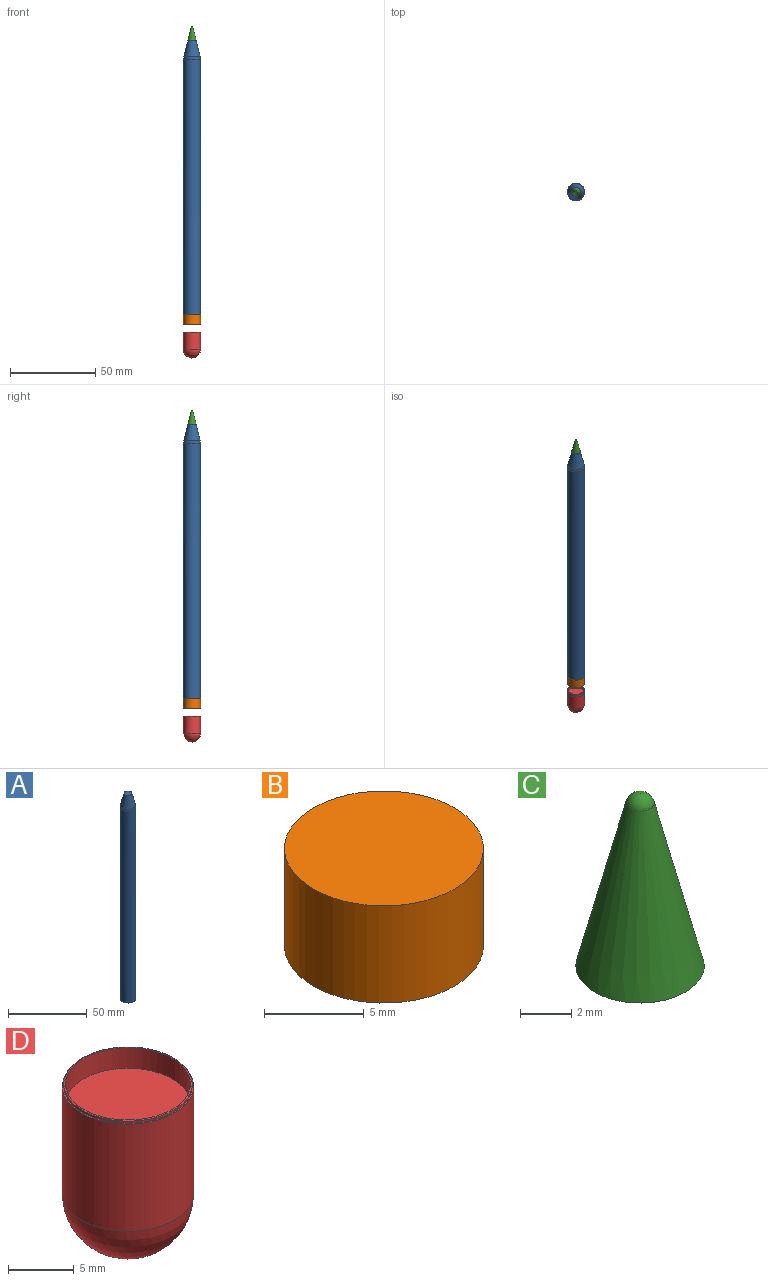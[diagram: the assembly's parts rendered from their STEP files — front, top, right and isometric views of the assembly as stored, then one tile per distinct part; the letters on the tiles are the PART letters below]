
ASSEMBLY  parts=4 mates=3
PART A: 5 faces, bbox 10x10x160 mm
  f0: cylinder r=5mm len=149.26mm, axis (0,0,-1), area 4689.2mm2, adj f1,f4
  f1: plane 10x10mm, normal (0,0,-1), area 78.5mm2, adj f0
  f2: plane 5x5mm, normal (0,0,1), area 19.6mm2, adj f3
  f3: cone r=5mm half-angle=14deg, axis (0,0,-1), area 220.1mm2, adj f2,f4
  f4: revolved ~10x10mm, area 91.2mm2, adj f0,f3
PART B: 106 faces, bbox 10x10x6 mm
  f0: cylinder r=5mm len=10mm, axis (0,0,-1), area 179.7mm2, adj f1,f6,f13,f14,f15,f16,f17,f18
  f1: plane 10x10mm, normal (0,0,1), area 78.5mm2, adj f0
  f2: plane 9.5x9.5mm, normal (0,0,-1), area 70.9mm2, adj f3
  f3: cylinder r=4.75mm len=9.5mm, axis (0,0,-1), area 5.4mm2, adj f2,f4
  f4: cone r=4.75mm half-angle=78.8deg, axis (0,0,-1), area 4.6mm2, adj f3,f5
  f5: cylinder r=4.9mm len=9.8mm, axis (0,0,-1), area 6.2mm2, adj f4,f6
  f6: cone r=4.9mm half-angle=76.3deg, axis (0,0,1), area 3.2mm2, adj f0,f5
  f7: plane 0.22x0.16mm, normal (0,0,1), area 0mm2, adj f8,f21,f22,f98
  f8: plane 0.84x0.15mm, normal (-1,0,0), area 0.1mm2, adj f7,f9,f22,f98
  f9: plane 0.27x0.16mm, normal (0,0,-1), area 0mm2, adj f8,f10,f22,f98
  f10: extruded ~0.42x0.15mm, area 0.1mm2, adj f9,f11,f22,f98
  f11: extruded ~0.3x0.15mm, area 0mm2, adj f10,f12,f22,f98
  f12: extruded ~0.33x0.15mm, area 0.1mm2, adj f11,f21,f22,f98
  f13: extruded ~0.48x0.21mm, area 0.1mm2, adj f0,f14,f20,f22
  f14: extruded ~0.77x0.6mm, area 0.2mm2, adj f0,f13,f15,f22
  f15: plane 0.54x0.19mm, normal (0,0,1), area 0.1mm2, adj f0,f14,f16,f22
  f16: plane 2.06x0.15mm, normal (1,0,0), area 0.3mm2, adj f0,f15,f17,f22
  f17: plane 0.24x0.18mm, normal (0,0,-1), area 0mm2, adj f0,f16,f18,f22
  f18: plane 0.81x0.15mm, normal (-1,0,0), area 0.1mm2, adj f0,f17,f19,f22
  f19: plane 0.24x0.16mm, normal (0,0,-1), area 0mm2, adj f0,f18,f20,f22
  f20: extruded ~0.61x0.17mm, area 0.1mm2, adj f0,f13,f19,f22
  f21: extruded ~0.46x0.14mm, area 0.1mm2, adj f7,f12,f22,f98
  f22: cylinder r=4.86mm len=2.06mm, axis (0,0,1), area 1mm2, adj f7,f8,f9,f10,f11,f12,f13,f14
  f23: plane 0.25x0.19mm, normal (0,0,-1), area 0mm2, adj f0,f24,f26,f27
  f24: plane 2.2x0.09mm, normal (-0.42,0.91,0), area 0.2mm2, adj f0,f23,f25,f27
  f25: plane 0.25x0.19mm, normal (0,0,1), area 0mm2, adj f0,f24,f26,f27
  f26: plane 2.2x0.09mm, normal (0.42,-0.91,0), area 0.2mm2, adj f0,f23,f25,f27
  f27: cylinder r=4.86mm len=2.2mm, axis (0,0,1), area 0.5mm2, adj f23,f24,f25,f26
  f28: extruded ~0.12x0.11mm, area 0mm2, adj f0,f29,f35,f36
  f29: extruded ~0.12x0.11mm, area 0mm2, adj f0,f28,f30,f36
  f30: extruded ~0.14x0.14mm, area 0mm2, adj f0,f29,f31,f36
  f31: extruded ~0.14x0.14mm, area 0mm2, adj f0,f30,f32,f36
  f32: extruded ~0.12x0.11mm, area 0mm2, adj f0,f31,f33,f36
  f33: extruded ~0.12x0.11mm, area 0mm2, adj f0,f32,f34,f36
  f34: extruded ~0.14x0.14mm, area 0mm2, adj f0,f33,f35,f36
  f35: extruded ~0.14x0.14mm, area 0mm2, adj f0,f28,f34,f36
  f36: cylinder r=4.86mm len=0.31mm, axis (0,0,1), area 0.1mm2, adj f28,f29,f30,f31,f32,f33,f34,f35
  f37: extruded ~0.32x0.22mm, area 0mm2, adj f38,f55,f56,f99
  f38: extruded ~0.31x0.21mm, area 0mm2, adj f37,f39,f56,f99
  f39: extruded ~0.34x0.16mm, area 0mm2, adj f38,f40,f56,f99
  f40: plane 0.81x0.34mm, normal (0,0,1), area 0.1mm2, adj f39,f55,f56,f99
  f41: extruded ~0.56x0.3mm, area 0.1mm2, adj f0,f42,f54,f56
  f42: extruded ~0.3x0.21mm, area 0mm2, adj f0,f41,f43,f56
  f43: extruded ~0.27x0.21mm, area 0mm2, adj f0,f42,f44,f56
  f44: plane 0.21x0.12mm, normal (-0.96,0.28,0), area 0mm2, adj f0,f43,f45,f56
  f45: extruded ~0.52x0.29mm, area 0.1mm2, adj f0,f44,f46,f56
  f46: extruded ~0.39x0.24mm, area 0.1mm2, adj f0,f45,f47,f56
  f47: extruded ~0.41x0.18mm, area 0.1mm2, adj f0,f46,f48,f56
  f48: plane 1.05x0.44mm, normal (0,0,-1), area 0.1mm2, adj f0,f47,f49,f56
  f49: plane 0.15x0.12mm, normal (-0.96,0.28,0), area 0mm2, adj f0,f48,f50,f56
  f50: extruded ~0.5x0.2mm, area 0.1mm2, adj f0,f49,f51,f56
  f51: extruded ~0.48x0.27mm, area 0.1mm2, adj f0,f50,f52,f56
  f52: extruded ~0.52x0.29mm, area 0.1mm2, adj f0,f51,f53,f56
  f53: extruded ~0.59x0.22mm, area 0.1mm2, adj f0,f52,f54,f56
  f54: extruded ~0.58x0.23mm, area 0.1mm2, adj f0,f41,f53,f56
  f55: extruded ~0.34x0.17mm, area 0mm2, adj f37,f40,f56,f99
  f56: cylinder r=4.86mm len=1.6mm, axis (0,0,1), area 0.9mm2, adj f37,f38,f39,f40,f41,f42,f43,f44
  f57: extruded ~0.16x0.15mm, area 0mm2, adj f0,f58,f75,f76
  f58: extruded ~0.17x0.16mm, area 0mm2, adj f0,f57,f59,f76
  f59: plane 0.11x0.08mm, normal (0,0,1), area 0mm2, adj f0,f58,f60,f76
  f60: plane 0.21x0.12mm, normal (-0.83,0.54,0.18), area 0mm2, adj f0,f59,f61,f76
  f61: plane 0.24x0.19mm, normal (0,0,1), area 0mm2, adj f0,f60,f62,f76
  f62: plane 1.55x0.1mm, normal (0.84,-0.54,0), area 0.2mm2, adj f0,f61,f63,f76
  f63: plane 0.28x0.21mm, normal (0,0,-1), area 0mm2, adj f0,f62,f64,f76
  f64: plane 0.81x0.1mm, normal (-0.84,0.54,0), area 0.1mm2, adj f0,f63,f65,f76
  f65: extruded ~0.43x0.17mm, area 0.1mm2, adj f0,f64,f66,f76
  f66: plane 0.1x0.07mm, normal (-0.64,0.41,-0.65), area 0mm2, adj f0,f65,f67,f76
  f67: extruded ~0.37x0.3mm, area 0mm2, adj f0,f66,f68,f76
  f68: extruded ~0.29x0.25mm, area 0mm2, adj f0,f67,f69,f76
  f69: extruded ~0.28x0.15mm, area 0mm2, adj f0,f68,f70,f76
  f70: plane 1x0.1mm, normal (0.84,-0.54,0), area 0.1mm2, adj f0,f69,f71,f76
  f71: plane 0.25x0.24mm, normal (0,0,-1), area 0mm2, adj f0,f70,f72,f76
  f72: plane 1.01x0.1mm, normal (-0.84,0.54,0), area 0.1mm2, adj f0,f71,f73,f76
  f73: extruded ~0.43x0.19mm, area 0.1mm2, adj f0,f72,f74,f76
  f74: extruded ~0.43x0.35mm, area 0.1mm2, adj f0,f73,f75,f76
  f75: extruded ~0.31x0.26mm, area 0mm2, adj f0,f57,f74,f76
  f76: cylinder r=4.86mm len=1.57mm, axis (0,0,1), area 0.9mm2, adj f57,f58,f59,f60,f61,f62,f63,f64
  f77: extruded ~0.48x0.43mm, area 0.1mm2, adj f0,f78,f91,f92
  f78: extruded ~0.38x0.35mm, area 0mm2, adj f0,f77,f79,f92
  f79: plane 0.21x0.08mm, normal (-0.64,0.77,0), area 0mm2, adj f0,f78,f80,f92
  f80: extruded ~0.38x0.35mm, area 0mm2, adj f0,f79,f81,f92
  f81: extruded ~0.34x0.31mm, area 0mm2, adj f0,f80,f82,f92
  f82: extruded ~0.44x0.16mm, area 0.1mm2, adj f0,f81,f83,f92
  f83: extruded ~0.6x0.44mm, area 0.1mm2, adj f0,f82,f84,f92
  f84: extruded ~0.2x0.19mm, area 0mm2, adj f0,f83,f85,f92
  f85: extruded ~0.2x0.2mm, area 0mm2, adj f0,f84,f86,f92
  f86: plane 0.2x0.13mm, normal (-0.6,0.72,-0.34), area 0mm2, adj f0,f85,f87,f92
  f87: extruded ~0.21x0.2mm, area 0mm2, adj f0,f86,f88,f92
  f88: extruded ~0.24x0.23mm, area 0mm2, adj f0,f87,f89,f92
  f89: extruded ~0.49x0.44mm, area 0.1mm2, adj f0,f88,f90,f92
  f90: extruded ~0.6x0.23mm, area 0.1mm2, adj f0,f89,f91,f92
  f91: extruded ~0.59x0.23mm, area 0.1mm2, adj f0,f77,f90,f92
  f92: cylinder r=4.86mm len=1.6mm, axis (0,0,1), area 0.6mm2, adj f77,f78,f79,f80,f81,f82,f83,f84
  f93: plane 0.25x0.21mm, normal (0,0,-1), area 0mm2, adj f0,f94,f96,f97
  f94: plane 1.55x0.09mm, normal (-0.52,0.86,0), area 0.2mm2, adj f0,f93,f95,f97
  f95: plane 0.25x0.21mm, normal (0,0,1), area 0mm2, adj f0,f94,f96,f97
  f96: plane 1.55x0.09mm, normal (0.52,-0.86,0), area 0.2mm2, adj f0,f93,f95,f97
  f97: cylinder r=4.86mm len=1.55mm, axis (0,0,1), area 0.4mm2, adj f93,f94,f95,f96
  f98: cylinder r=5mm len=0.84mm, axis (0,0,-1), area 0.6mm2, adj f7,f8,f9,f10,f11,f12,f21
  f99: cylinder r=5mm len=0.78mm, axis (0,0,-1), area 0.3mm2, adj f37,f38,f39,f40,f55
  f100: cylinder r=0.53mm len=0.93mm, axis (0.34,-0.94,0), area 0.3mm2, adj f0,f101,f102
  f101: extruded ~1.86x1.73mm, area 1.3mm2, adj f0,f100,f102
  f102: cylinder r=4.75mm len=1.73mm, axis (0,0,1), area 2.5mm2, adj f100,f101
  f103: cylinder r=0.49mm len=0.5mm, axis (0.34,-0.94,0), area 0.2mm2, adj f0,f104,f105
  f104: cylinder r=0.46mm len=0.5mm, axis (0.34,-0.94,0), area 0.2mm2, adj f0,f103,f105
  f105: cylinder r=4.75mm len=0.5mm, axis (0,0,1), area 0.1mm2, adj f103,f104
PART C: 5 faces, bbox 5x5x8.7 mm
  f0: plane 5x5mm, normal (0,0,-1), area 12.6mm2, adj f1,f4
  f1: cylinder r=1.5mm len=3mm, axis (0,0,1), area 4.7mm2, adj f0,f2
  f2: plane 3x3mm, normal (0,0,-1), area 7.1mm2, adj f1
  f3: sphere r=0.57mm, area 1.6mm2, adj f4
  f4: cone r=2.5mm half-angle=14deg, axis (0,0,-1), area 77mm2, adj f0,f3
PART D: 11 faces, bbox 10x10x15.2 mm
  f0: sphere r=5mm, area 134.4mm2, adj f4,f8
  f1: cone r=4.89mm half-angle=80deg, axis (0,0,-1), area 3.9mm2, adj f2,f6
  f2: cylinder r=4.76mm len=9.52mm, axis (0,0,-1), area 57.2mm2, adj f1,f3
  f3: plane 9.52x9.52mm, normal (0,0,1), area 71.2mm2, adj f2
  f4: cylinder r=5mm len=10mm, axis (0,0,-1), area 313.8mm2, adj f0,f5
  f5: plane 10x10mm, normal (0,0,1), area 3.5mm2, adj f4,f6
  f6: cylinder r=4.89mm len=9.78mm, axis (0,0,-1), area 6.1mm2, adj f1,f5
  f7: cylinder r=2.37mm len=4.75mm, axis (0,0,1), area 66.6mm2, adj f9,f10
  f8: cylinder r=2.59mm len=5.18mm, axis (0,0,1), area 70.7mm2, adj f0,f9
  f9: plane 5.18x5.18mm, normal (0,0,-1), area 3.3mm2, adj f7,f8
  f10: sphere r=5mm, area 18.8mm2, adj f7
PLACE A t=(8.92,0,-54.57)mm
PLACE B t=(8.92,0,-54.57)mm
PLACE C t=(8.92,0,-54.17)mm
PLACE D t=(8.87,0,-56.73)mm
MATE fastened A.f0 <-> B.f0  axis (0,0,-1) through (8.92,0,-129.57)mm
MATE cylindrical C.f1 <-> A.f3  axis (0,0,-1) through (8.92,0,30.43)mm
MATE cylindrical B.f0 <-> D.f1  axis (0,0,1) through (8.92,0,-135.57)mm
